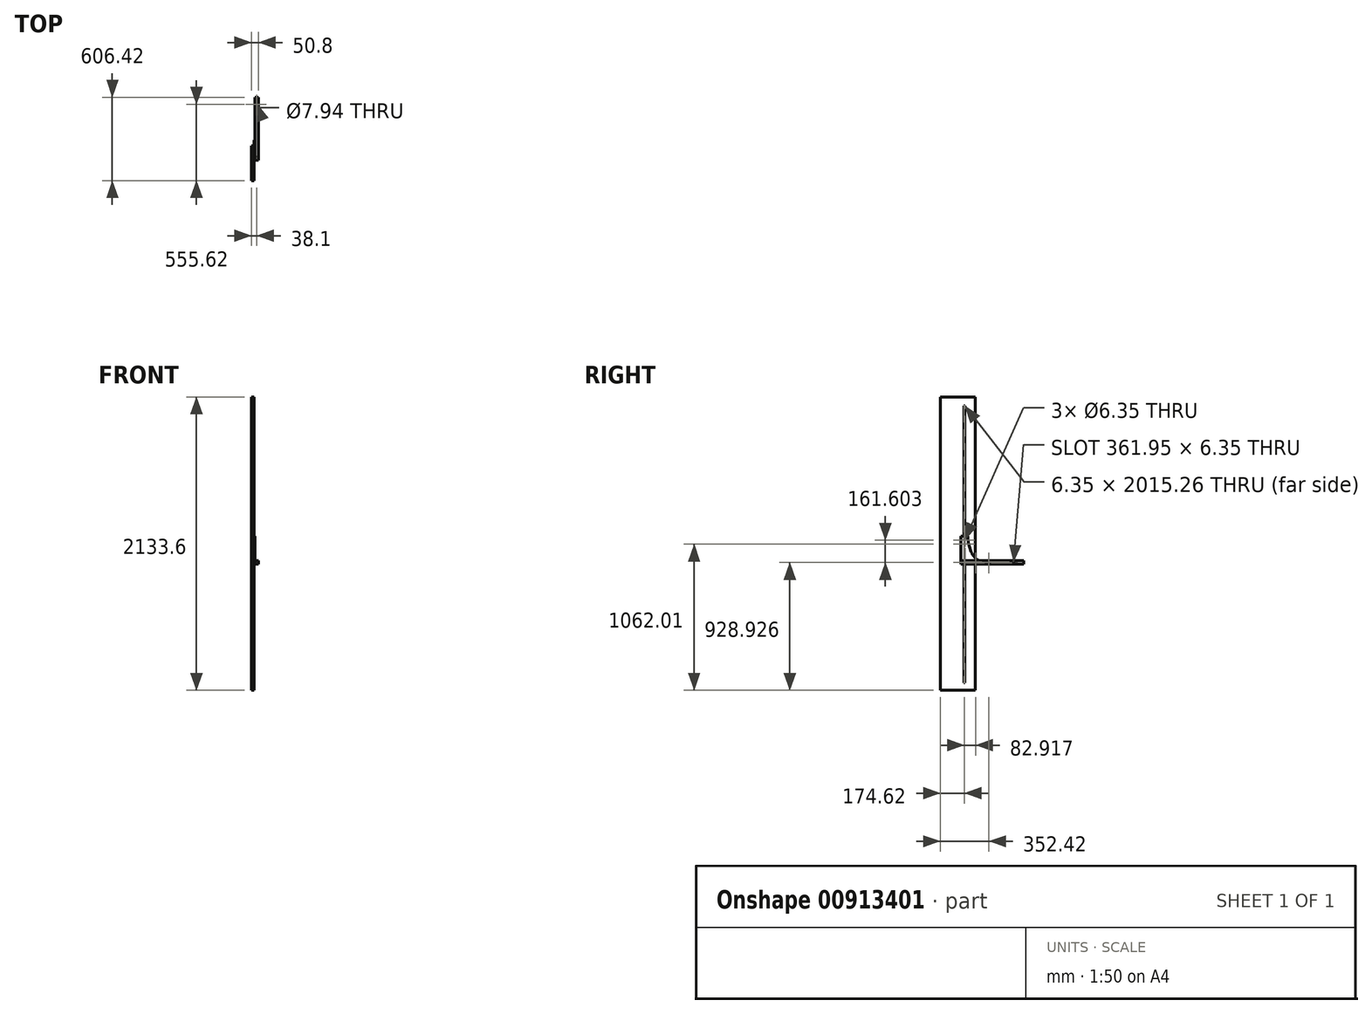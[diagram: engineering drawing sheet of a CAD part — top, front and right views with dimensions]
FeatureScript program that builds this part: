
annotation { "Feature Type Name" : "Feature", "Feature Type Description" : "" }
export const myFeature = defineFeature(function(context is Context, id is Id, definition is map)
    precondition{}
    {
        {
            var Q0;
            Q0=qCreatedBy(makeId("Right.planeOp"),FACE);
            var sketch = newSketch(context, id + "F0", { "sketchPlane" : qUnion([Q0])});
            skLineSegment(sketch, "E0.bottom", {"start": v(-148.95, 1062.62) * mm, "end": v(105.05, 1062.62) * mm});
            skLineSegment(sketch, "E0.top", {"start": v(-148.95, -1070.98) * mm, "end": v(105.05, -1070.98) * mm});
            skLineSegment(sketch, "E0.left", {"start": v(-148.95, 1062.62) * mm, "end": v(-148.95, -1070.98) * mm});
            skLineSegment(sketch, "E0.right", {"start": v(105.05, 1062.62) * mm, "end": v(105.05, -1070.98) * mm});
            skLineSegment(sketch, "E1.bottom", {"start": v(22.5, 998.66) * mm, "end": v(28.85, 998.66) * mm});
            skLineSegment(sketch, "E1.top", {"start": v(22.5, -1016.6) * mm, "end": v(28.85, -1016.6) * mm});
            skLineSegment(sketch, "E1.left", {"start": v(22.5, 998.66) * mm, "end": v(22.5, -1016.6) * mm});
            skLineSegment(sketch, "E1.right", {"start": v(28.85, 998.66) * mm, "end": v(28.85, -1016.6) * mm});
            skSolve(sketch);
        }
        {
            var Q0;
            Q0=makeQuery(id+"F0.imprint","IMPRINT",FACE,{"disambiguationData":[TD([[makeQuery(id+"F0.imprint","IMPRINT",EDGE,{"derivedFrom":sQuery(id+"F0.wireOp",EDGE,"E0.bottom")}),-1.0]])]});
            extrude(context, id + "F1", {"entities" : qUnion([Q0]), "depth" : 19.05 * mm, "offsetDistance" : 25.4 * mm});
        }
        {
            var Q0;
            Q0=makeQuery(id+"F1.opExtrude","CAP_FACE",FACE,{"disambiguationData":[OSD([sQuery(id+"F0.wireOp",EDGE,"E0.bottom"),sQuery(id+"F0.wireOp",EDGE,"E0.top"),sQuery(id+"F0.wireOp",EDGE,"E0.left"),sQuery(id+"F0.wireOp",EDGE,"E0.right"),sQuery(id+"F0.wireOp",EDGE,"E1.bottom"),sQuery(id+"F0.wireOp",EDGE,"E1.top"),sQuery(id+"F0.wireOp",EDGE,"E1.left"),sQuery(id+"F0.wireOp",EDGE,"E1.right")])],"isStart":false});
            var sketch = newSketch(context, id + "F2", { "sketchPlane" : qUnion([Q0])});
            skLineSegment(sketch, "E2.bottom", {"start": v(0.27, 48.45) * mm, "end": v(51.07, 48.45) * mm});
            skLineSegment(sketch, "E2.top", {"start": v(0.27, -154.75) * mm, "end": v(51.07, -154.75) * mm});
            skLineSegment(sketch, "E2.left", {"start": v(0.27, 48.45) * mm, "end": v(0.27, -154.75) * mm});
            skLineSegment(sketch, "E3.0", {"start": v(28.85, 998.66) * mm, "end": v(28.85, -1016.6) * mm, "construction": true});
            skLineSegment(sketch, "E3.1", {"start": v(22.5, 998.66) * mm, "end": v(22.5, -1016.6) * mm, "construction": true});
            skCircle(sketch, "E4", {"center": v(25.67, 19.55) * mm, "radius": 3.18 * mm});
            skCircle(sketch, "E5", {"center": v(25.67, -142.05) * mm, "radius": 3.18 * mm});
            skLineSegment(sketch, "E6", {"start": v(144.5, -129.35) * mm, "end": v(144.5, -154.75) * mm});
            skLineSegment(sketch, "E7", {"start": v(144.5, -154.75) * mm, "end": v(51.07, -154.75) * mm});
            skCircle(sketch, "E8", {"center": v(108.59, -142.05) * mm, "radius": 3.18 * mm});
            skFitSpline(sketch, "E9", {"points": [v(51.07, 48.45) * mm, v(144.5, -129.35) * mm], "startDerivative": vector(0, -266.7) * mm, "endDerivative": vector(140.16, 0) * mm});
            skPoint(sketch, "E10.start.orphan", {"position": v(51.07, -129.35) * mm});
            skSolve(sketch);
        }
        {
            var Q0;
            Q0 = qSketchRegion(id + "F2", true);
            extrude(context, id + "F3", {"entities" : qUnion([Q0]), "depth" : 6.35 * mm, "offsetDistance" : 25.4 * mm});
        }
        {
            var Q0;
            Q0=makeQuery(id+"F3.opExtrude","CAP_FACE",FACE,{"disambiguationData":[OSD([sQuery(id+"F2.wireOp",EDGE,"E2.bottom"),sQuery(id+"F2.wireOp",EDGE,"E2.top"),sQuery(id+"F2.wireOp",EDGE,"E2.left"),sQuery(id+"F2.wireOp",EDGE,"E2.right"),sQuery(id+"F2.wireOp",EDGE,"E4"),sQuery(id+"F2.wireOp",EDGE,"E5"),sQuery(id+"F2.wireOp",EDGE,"E10"),sQuery(id+"F2.wireOp",EDGE,"E6"),sQuery(id+"F2.wireOp",EDGE,"E7"),sQuery(id+"F2.wireOp",EDGE,"E8")])],"isStart":false});
            var sketch = newSketch(context, id + "F4", { "sketchPlane" : qUnion([Q0])});
            skLineSegment(sketch, "E11.bottom", {"start": v(0.27, -129.35) * mm, "end": v(457.47, -129.35) * mm});
            skLineSegment(sketch, "E11.top", {"start": v(0.27, -154.75) * mm, "end": v(457.47, -154.75) * mm});
            skLineSegment(sketch, "E11.left", {"start": v(0.27, -129.35) * mm, "end": v(0.27, -154.75) * mm});
            skLineSegment(sketch, "E11.right", {"start": v(457.47, -129.35) * mm, "end": v(457.47, -154.75) * mm});
            skArc(sketch, "E12.0", {"start": v(25.67, -138.88) * mm, "mid": v(22.5, -142.1) * mm, "end": v(25.77, -145.23) * mm});
            skLineSegment(sketch, "E13", {"start": v(25.67, -138.88) * mm, "end": v(381.27, -138.88) * mm});
            skLineSegment(sketch, "E14", {"start": v(25.77, -145.23) * mm, "end": v(381.27, -145.23) * mm});
            skArc(sketch, "E15", {"start": v(381.27, -145.23) * mm, "mid": v(384.44, -142.05) * mm, "end": v(381.27, -138.88) * mm});
            skSolve(sketch);
        }
        {
            var Q0;
            Q0 = qSketchRegion(id + "F4", true);
            extrude(context, id + "F5", {"entities" : qUnion([Q0]), "depth" : 25.4 * mm, "offsetDistance" : 25.4 * mm});
        }
        {
            var Q0;
            Q0=makeQuery(id+"F5.opExtrude","SWEPT_FACE",FACE,{"disambiguationData":[OSD([sQuery(id+"F4.wireOp",EDGE,"E11.bottom")])]});
            var sketch = newSketch(context, id + "F6", { "sketchPlane" : qUnion([Q0])});
            skCircle(sketch, "E16", {"center": v(38.1, 406.67) * mm, "radius": 3.97 * mm});
            skPoint(sketch, "E16.centerSnap0", {"position": v(38.1, 457.47) * mm});
            skSolve(sketch);
        }
        {
            var Q0;
            Q0 = qSketchRegion(id + "F6", true);
            extrude(context, id + "F7", {"entities" : qUnion([Q0]), "operationType" : NewBodyOperationType.REMOVE, "oppositeDirection" : true, "depth" : 25.4 * mm, "offsetDistance" : 25.4 * mm});
        }
    });
